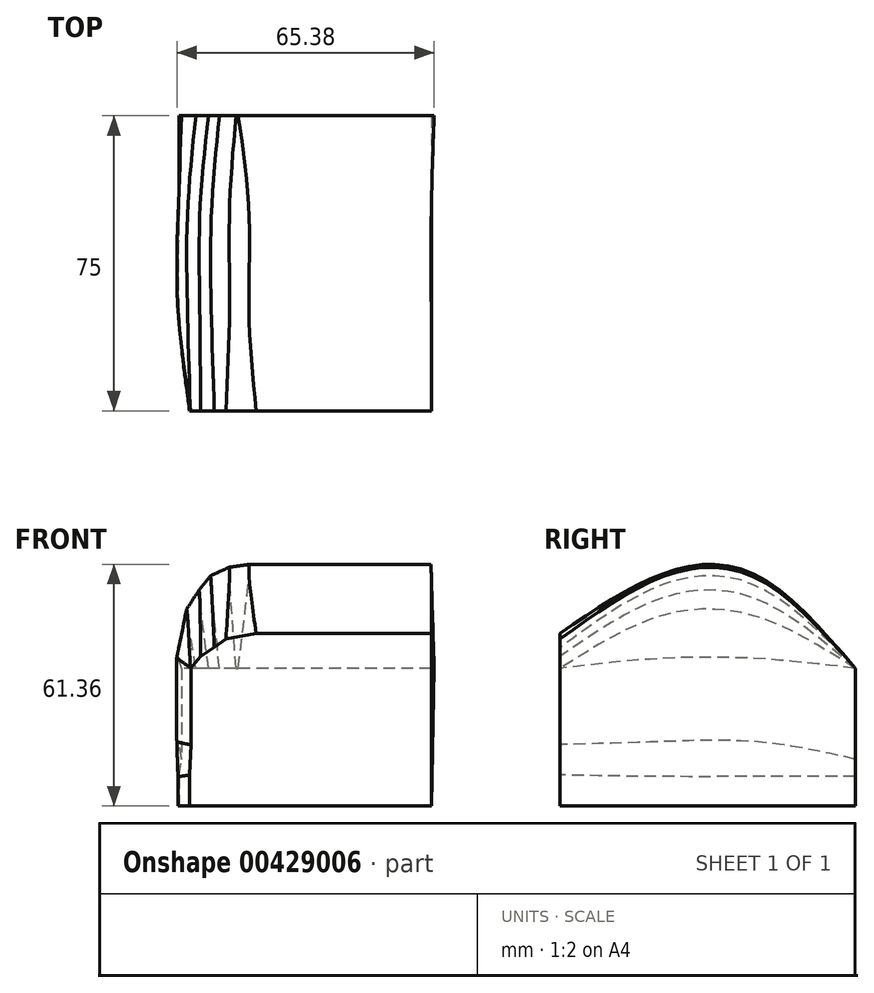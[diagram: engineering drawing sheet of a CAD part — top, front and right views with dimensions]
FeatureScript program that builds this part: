
annotation { "Feature Type Name" : "Feature", "Feature Type Description" : "" }
export const myFeature = defineFeature(function(context is Context, id is Id, definition is map)
    precondition{}
    {
        {
            var Q0;
            Q0=qCreatedBy(makeId("Front.planeOp"),FACE);
            cPlane(context, id + "F0", {"entities" : qUnion([Q0]), "cplaneType" : CPlaneType.OFFSET, "offset" : 25 * mm, "width" : 150 * mm, "height" : 150 * mm});
        }
        {
            var Q0;
            Q0=qCreatedBy(id+"F0.planeOp",FACE);
            cPlane(context, id + "F1", {"entities" : qUnion([Q0]), "cplaneType" : CPlaneType.OFFSET, "offset" : 25 * mm, "width" : 150 * mm, "height" : 150 * mm});
        }
        {
            var Q0;
            Q0=qCreatedBy(id+"F1.planeOp",FACE);
            cPlane(context, id + "F2", {"entities" : qUnion([Q0]), "cplaneType" : CPlaneType.OFFSET, "offset" : 25 * mm, "width" : 150 * mm, "height" : 150 * mm});
        }
        {
            var Q0;
            Q0=qCreatedBy(id+"F2.planeOp",FACE);
            cPlane(context, id + "F3", {"entities" : qUnion([Q0]), "cplaneType" : CPlaneType.OFFSET, "offset" : 25 * mm, "width" : 150 * mm, "height" : 150 * mm});
        }
        {
            var Q0;
            Q0=qCreatedBy(id+"F3.planeOp",FACE);
            cPlane(context, id + "F4", {"entities" : qUnion([Q0]), "cplaneType" : CPlaneType.OFFSET, "offset" : 25 * mm, "width" : 150 * mm, "height" : 150 * mm});
        }
        {
            var Q0;
            Q0=qCreatedBy(id+"F1.planeOp",FACE);
            var sketch = newSketch(context, id + "F5", { "sketchPlane" : qUnion([Q0])});
            skLineSegment(sketch, "E0", {"start": v(50.36, 0) * mm, "end": v(0.57, 0) * mm});
            skLineSegment(sketch, "E1", {"start": v(0, 0) * mm, "end": v(0.57, 0) * mm});
            skLineSegment(sketch, "E2", {"start": v(0, 0) * mm, "end": v(-4.23, 0) * mm});
            skLineSegment(sketch, "E3", {"start": v(-4.23, 0) * mm, "end": v(-6.97, 0) * mm});
            skLineSegment(sketch, "E4", {"start": v(-6.97, 0) * mm, "end": v(-10.18, 0) * mm});
            skLineSegment(sketch, "E5", {"start": v(-10.18, 0) * mm, "end": v(-13.78, 0) * mm});
            skLineSegment(sketch, "E6", {"start": v(-13.78, 0) * mm, "end": v(-13.78, -7.84) * mm});
            skLineSegment(sketch, "E7", {"start": v(-13.78, -7.84) * mm, "end": v(-13.78, -23.09) * mm});
            skLineSegment(sketch, "E8", {"start": v(-14.52, -27.5) * mm, "end": v(-13.78, -23.09) * mm});
            skLineSegment(sketch, "E9", {"start": v(-14.52, -27.5) * mm, "end": v(-14.52, -34.95) * mm});
            skLineSegment(sketch, "E10", {"start": v(-14.52, -34.95) * mm, "end": v(49.62, -34.95) * mm});
            skLineSegment(sketch, "E11", {"start": v(49.62, -34.95) * mm, "end": v(50.36, 0) * mm});
            skSolve(sketch);
        }
        {
            var Q0;
            Q0=qCreatedBy(id+"F2.planeOp",FACE);
            var sketch = newSketch(context, id + "F6", { "sketchPlane" : qUnion([Q0])});
            skLineSegment(sketch, "E12", {"start": v(49.62, 23.59) * mm, "end": v(3.3, 23.59) * mm});
            skLineSegment(sketch, "E13", {"start": v(3.3, 23.59) * mm, "end": v(-1.65, 22.85) * mm});
            skLineSegment(sketch, "E14", {"start": v(-1.65, 22.85) * mm, "end": v(-6.25, 20.83) * mm});
            skLineSegment(sketch, "E15", {"start": v(-6.25, 20.83) * mm, "end": v(-9.19, 17.52) * mm});
            skLineSegment(sketch, "E16", {"start": v(-9.19, 17.52) * mm, "end": v(-12.31, 13.1) * mm});
            skLineSegment(sketch, "E17", {"start": v(-12.31, 13.1) * mm, "end": v(-14.7, 2.45) * mm});
            skLineSegment(sketch, "E18", {"start": v(-14.7, 2.45) * mm, "end": v(-14.7, -7.84) * mm});
            skLineSegment(sketch, "E19", {"start": v(-14.7, -7.84) * mm, "end": v(-14.7, -18.68) * mm});
            skLineSegment(sketch, "E20", {"start": v(-14.7, -18.68) * mm, "end": v(-14.52, -27.5) * mm});
            skLineSegment(sketch, "E21", {"start": v(-14.52, -27.5) * mm, "end": v(-14.52, -34.95) * mm});
            skLineSegment(sketch, "E22", {"start": v(-14.52, -34.95) * mm, "end": v(49.62, -34.95) * mm});
            skLineSegment(sketch, "E23", {"start": v(49.62, -34.95) * mm, "end": v(49.62, 23.59) * mm});
            skSolve(sketch);
        }
        {
            var Q0;
            Q0=qCreatedBy(id+"F3.planeOp",FACE);
            var sketch = newSketch(context, id + "F7", { "sketchPlane" : qUnion([Q0])});
            skLineSegment(sketch, "E24", {"start": v(49.62, 23.59) * mm, "end": v(3.3, 23.59) * mm});
            skLineSegment(sketch, "E25", {"start": v(3.3, 23.59) * mm, "end": v(-1.65, 22.85) * mm});
            skLineSegment(sketch, "E26", {"start": v(-1.65, 22.85) * mm, "end": v(-6.25, 20.83) * mm});
            skLineSegment(sketch, "E27", {"start": v(-6.25, 20.83) * mm, "end": v(-9.19, 17.52) * mm});
            skLineSegment(sketch, "E28", {"start": v(-9.19, 17.52) * mm, "end": v(-12.31, 13.1) * mm});
            skLineSegment(sketch, "E29", {"start": v(-12.31, 13.1) * mm, "end": v(-14.7, 2.45) * mm});
            skLineSegment(sketch, "E30", {"start": v(-14.7, 2.45) * mm, "end": v(-14.7, -7.84) * mm});
            skLineSegment(sketch, "E31", {"start": v(-14.7, -7.84) * mm, "end": v(-14.7, -18.68) * mm});
            skLineSegment(sketch, "E32", {"start": v(-14.7, -18.68) * mm, "end": v(-14.52, -27.5) * mm});
            skLineSegment(sketch, "E33", {"start": v(-14.52, -27.5) * mm, "end": v(-14.52, -34.95) * mm});
            skLineSegment(sketch, "E34", {"start": v(-14.52, -34.95) * mm, "end": v(49.62, -34.95) * mm});
            skLineSegment(sketch, "E35", {"start": v(49.62, -34.95) * mm, "end": v(49.62, 23.59) * mm});
            skSolve(sketch);
        }
        {
            var Q0;
            Q0=qCreatedBy(id+"F4.planeOp",FACE);
            var sketch = newSketch(context, id + "F8", { "sketchPlane" : qUnion([Q0])});
            skLineSegment(sketch, "E36", {"start": v(49.62, 8.91) * mm, "end": v(5.15, 8.91) * mm});
            skLineSegment(sketch, "E37", {"start": v(5.15, 8.91) * mm, "end": v(-2.57, 7.44) * mm});
            skLineSegment(sketch, "E38", {"start": v(-2.57, 7.44) * mm, "end": v(-5.51, 5.24) * mm});
            skLineSegment(sketch, "E39", {"start": v(-5.51, 5.24) * mm, "end": v(-9, 3.03) * mm});
            skLineSegment(sketch, "E40", {"start": v(-9, 3.03) * mm, "end": v(-11.58, 0) * mm});
            skLineSegment(sketch, "E41", {"start": v(-11.4, 0) * mm, "end": v(-11.58, 0) * mm});
            skLineSegment(sketch, "E42", {"start": v(-11.4, 0) * mm, "end": v(-11.4, -7.84) * mm});
            skLineSegment(sketch, "E43", {"start": v(-11.4, -7.84) * mm, "end": v(-11.4, -19.39) * mm});
            skLineSegment(sketch, "E44", {"start": v(-11.76, -27.1) * mm, "end": v(-11.4, -19.39) * mm});
            skLineSegment(sketch, "E45", {"start": v(-11.76, -27.1) * mm, "end": v(-11.76, -34.95) * mm});
            skLineSegment(sketch, "E46", {"start": v(-11.76, -34.95) * mm, "end": v(49.62, -34.95) * mm});
            skLineSegment(sketch, "E47", {"start": v(49.62, -34.95) * mm, "end": v(49.62, 8.91) * mm});
            skSolve(sketch);
        }
        {
            var Q0;
            Q0 = qSketchRegion(id + "F5", true);
            var Q1;
            Q1 = qSketchRegion(id + "F6", true);
            var Q2;
            Q2 = qSketchRegion(id + "F7", true);
            var Q3;
            Q3 = qSketchRegion(id + "F8", true);
            loft(context, id + "F9", {"sheetProfilesArray" : [{ "sheetProfileEntities" : qUnion([Q0]) }, { "sheetProfileEntities" : qUnion([Q1]) }, { "sheetProfileEntities" : qUnion([Q2]) }, { "sheetProfileEntities" : qUnion([Q3]) }]});
        }
    });
